# Revit family: Electronics_Huddle-Room-Solutions_Biamp_Devio_Conferencing-Hub_SCR-20__
name_source: partatom
category: Communication Devices
units: mm (PartAtom-declared; Revit-internal decimal feet)

## family parameters
Cut with Voids When Loaded = No
Host = Face
Maintain Annotation Orientation = No
OmniClass Number = 23.85.10.17.11.11
OmniClass Title = Broadcasting Receiving Equipment
Part Type = Normal
Room Calculation Point = No
Round Connector Dimension = Use Diameter
Shared = No

## types (1)
- SCR-20
    Altitude = 0-6,600 ft (0-2000m) MSL
    Apparent Load = 60 VA
    Audio D/A Converters = 24-bit
    Audio Dynamic Range = THD+N < 0.005%: 107 dB, A-Weighted
    Audio Frequency Response = 20 Hz - 20 kHz, FS: +0/-0.25 dB
    Audio Maximum Output = +8.5 dBu
    Audio Output Impedance = 100 ohm (unbalanced)
    Audio Sampling Rate = 48 kHz
    Audio THD+N = 20 Hz - 10 kHz, 20 kHz B/W, FS: < 0.005%
    Compliance = FCC Part 15B (USA) UL and C-UL listed (USA and Canada) CE Marked (Europe) RoHS Directive (Europe)
    Connector Description = 24V DC 60W
    Continuous Power Output = THD+N < 0.025%: 20 W into Rated Load Impedance
    Default Elevation = 4' - 0"
    Depth = 0' - 6 29/32"
    Description = Devio® SCR-20 Conferencing Hub
    Dynamic Range = THD+N < 0.5%: 100 dB, A-Weighted
    Frequency Response = 20 Hz - 20 kHz, FS: +0/-0.25 dB
    HDCP Support = 1.4
    HDMI Audio Formats = 2ch L-PCM, 44.1 kHz/48 kHz, 16-bit
    Height = 0' - 1 13/16"
    Housing Material = Biamp - Plastic - Black
    Humidity = 0-95% relative humidity (non-condensing)
    Indicators = Mic Status Indicator (Green/Red LED) Room Tuning Indicator (Green/Red LED) Power Indicator (Green/Red LED)
    Intermodulation distortion = SMPTE, 60 Hz/7 kHz, 4:1, 1W: < 0.07%
    Manufacturer = Biamp
    Max Power Consumption = 60 W
    Minimum Operational Load = 4 ohm
    Model = Devio SCR-20
    Network Connection = RJ-45 with Ethernet cable (Cat 5e and above)
    Number of Channels = 1
    Number of Poles = 1
    Physical Interfaces = HDMI
    Power Factor = 1
    Product Documentation Link = https://downloads.biamp.com
    Product Page URL = https://www.biamp.com
    Product data url = https://www.bimobject.com
    SNMP = See support website for the full list of attributes
    Supported Resolutions = 640 x 480p (60 Hz); 720 x 480p (60 Hz); 720 x 576p (50 Hz); 1280 x 720p (50/60 Hz); 1920 x 1080p (50/60 Hz); 3840 x 2160p (30 Hz) - Supported on Output Port 1 only
    THD+N = 1 kHz, 20 kHz bandwidth, 1 W: < 0.03%
    Temperature Range = 32 - 104° F (0 – 40° C)
    URL = https://www.biamp.com
    USB Bit Depth = 24-bit
    USB Device Charging = Up to 5 W - Requires USB connection to computer
    USB Sample Rate = 48 kHz
    Voltage = 24 V
    Weight = 2.00 lbf
    Width = 0' - 11 3/16"

## geometry (parser evidence)
native form markers: Sweep x2
no freeform markers — native parametric forms only
